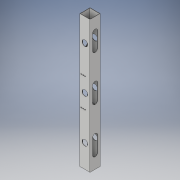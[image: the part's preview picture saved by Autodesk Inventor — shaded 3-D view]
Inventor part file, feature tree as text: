
AUTODESK INVENTOR PART (.ipt)
format: ipt  version: 2018 (Build 220112000, 112)  size: 216,064 bytes
history: native  units: in
note: dims shown in document units (in); Inventor stores cm internally (conversion verified against a paired STEP export)
features: extrude x6, sketch x6
ambient origin geometry x8: Origin, YZ Plane, XZ Plane, XY Plane, X Axis, Y Axis, Z Axis, Center Point
bodies: Solid1 (feature_tree)
feature tree (12):
  extrude  "Extrusion1"  Depth=2.0in
  extrude  "Extrusion2"  Depth=0.0625in
  extrude  "Extrusion3"  Depth=0.0625in
  extrude  "Extrusion4"  Depth=26.0in
  extrude  "Extrusion5"  Depth=20.875in TaperAngle=0.0deg
  extrude  "Extrusion6"  Depth=1.0in
  sketch  "Sketch1"  dims[d0=2.0in d1=2.0in]
  sketch  "Sketch2"  dims[d2=0.0625in d3=0.0625in]
  sketch  "Sketch3"  dims[d4=0.0625in d5=0.0625in]
  sketch  "Sketch4"  dims[d6=26.0in d7=0.0in d8=4.125in]
  sketch  "Sketch5"  dims[d9=4.125in d11=20.875in d12=0.0in]
  sketch  "Sketch6"  dims[d15=0.2in d16=0.375in d17=0.375in d18=4.0in d19=0.0in d20=1.0in d21=1.0in d22=2.625in d25=1.0in d27=1.0in d28=3.0in d29=5.0in d30=0.0in d31=1.0in d32=1.0in d33=2.625in d34=1.0in d35=1.0in d36=3.0in d37=5.0in d38=0.0in d39=1.0in d40=1.0in d41=1.0in d42=1.0in d43=11.5in d44=3.0in d45=5.0in d46=0.0in d47=8.4646in d48=8.4646in d49=0.978in d50=0.375in d51=0.375in d52=2.844in d53=0.978in d54=2.844in]
